# Revit family: Door_Access_Floor_Acudor_FT-8080-LiftOut
name_source: partatom
category: Generic Models
units: mm (PartAtom-declared; Revit-internal decimal feet)

## family parameters
Can host rebar = No
Cut with Voids When Loaded = No
Host = Face
Part Type = Normal
Room Calculation Point = No
Round Connector Dimension = Use Diameter
Shared = No

## types (8) — shared parameters
Capacity = 150 lbs/sqft
Default Elevation = 0' - 0"
Green Building-LEED = http://www.arcat.com
Manufacturer = Acudor Products Inc
Manufacturer Fax = 973-575-5160
Manufacturer Website = http://www.acudor.com
Product Data = http://www.arcat.com
Revision = R1_2017-03
Sales Information = http://www.acudor.com
Standards Conformance = as Specified
URL = http://www.acudor.com
Unit Depth = 0' - 2"
zero-valued in all types: Expected Lifespan (Years), Maintenance Schedule (Months), Warranty Duration (Years)

## per-type parameters (varying)
| type | Clear Opening Height | Clear Opening Width | Description | Door Height | Door Width | Model | Opening Height | Opening Width | Overall Height | Overall Width | Unit Height | Unit Weight | Unit Width | halfswing |
| 24 x 24 Nom for Tile or Concrete | 2' - 0" | 2' - 0" | Acudor Lift Out Floor Access Door for Tile or Concrete - FT8080-1 as Specified | 2' - 0 3/4" | 2' - 0 3/4" | FT-8080-1 | 2' - 0 3/4" | 2' - 0 3/4" | 2' - 3 1/4" | 2' - 3 1/4" | 2' - 0 3/4" | 36 | 2' - 0 3/4" | 1' - 0 3/8" |
| 18 x 18 Nom for Tile or Concrete | 1' - 6" | 1' - 6" | Acudor Lift Out Floor Access Door for Tile or Concrete - FT8080-1 as Specified | 1' - 6 3/4" | 1' - 6 3/4" | FT-8080-1 | 1' - 6 3/4" | 1' - 6 3/4" | 1' - 9 1/4" | 1' - 9 1/4" | 1' - 6 3/4" | 18 | 1' - 6 3/4" | 0' - 9 3/8" |
| 12 x 12 Nom for Tile or Concrete | 1' - 0" | 1' - 0" | Acudor Lift Out Floor Access Door for Tile or Concrete - FT8080-1 as Specified | 1' - 0 3/4" | 1' - 0 3/4" | FT-8080-1 | 1' - 0 3/4" | 1' - 0 3/4" | 1' - 3 1/4" | 1' - 3 1/4" | 1' - 0 3/4" | 9 | 1' - 0 3/4" | 0' - 6 3/8" |
| 8 x 8 Nom for Tile or Concrete | 0' - 8" | 0' - 8" | Acudor Lift Out Floor Access Door for Tile or Concrete - FT8080-1 as Specified | 0' - 8 3/4" | 0' - 8 3/4" | FT-8080-1 | 0' - 8 3/4" | 0' - 8 3/4" | 0' - 11 1/4" | 0' - 11 1/4" | 0' - 8 3/4" | 6 | 0' - 8 3/4" | 0' - 4 3/8" |
| 24 x 24 Nom for Vinyl Tile or Carpet | 2' - 0" | 2' - 0" | Acudor Lift Out Floor Access Door for Vinyl Tile or Carpet - FT8080 as Specified | 2' - 0 3/4" | 2' - 0 3/4" | FT-8080 | 2' - 0 3/4" | 2' - 0 3/4" | 2' - 3 1/4" | 2' - 3 1/4" | 2' - 0 3/4" | 36 | 2' - 0 3/4" | 1' - 0 3/8" |
| 18 x 18 Nom for Vinyl Tile or Carpet | 1' - 6" | 1' - 6" | Acudor Lift Out Floor Access Door for Vinyl Tile or Carpet - FT8080 as Specified | 1' - 6 3/4" | 1' - 6 3/4" | FT-8080 | 1' - 6 3/4" | 1' - 6 3/4" | 1' - 9 1/4" | 1' - 9 1/4" | 1' - 6 3/4" | 18 | 1' - 6 3/4" | 0' - 9 3/8" |
| 12 x 12 Nom for Vinyl Tile or Carpet | 1' - 0" | 1' - 0" | Acudor Lift Out Floor Access Door for Vinyl Tile or Carpet - FT8080 as Specified | 1' - 0 3/4" | 1' - 0 3/4" | FT-8080 | 1' - 0 3/4" | 1' - 0 3/4" | 1' - 3 1/4" | 1' - 3 1/4" | 1' - 0 3/4" | 9 | 1' - 0 3/4" | 0' - 6 3/8" |
| 8 x 8 Nom for Vinyl Tile or Carpet | 0' - 8" | 0' - 8" | Acudor Lift Out Floor Access Door for Vinyl Tile or Carpet - FT8080 as Specified | 0' - 8 3/4" | 0' - 8 3/4" | FT-8080 | 0' - 8 3/4" | 0' - 8 3/4" | 0' - 11 1/4" | 0' - 11 1/4" | 0' - 8 3/4" | 6 | 0' - 8 3/4" | 0' - 4 3/8" |

## geometry (parser evidence)
native form markers: Sweep x2
no freeform markers — native parametric forms only
